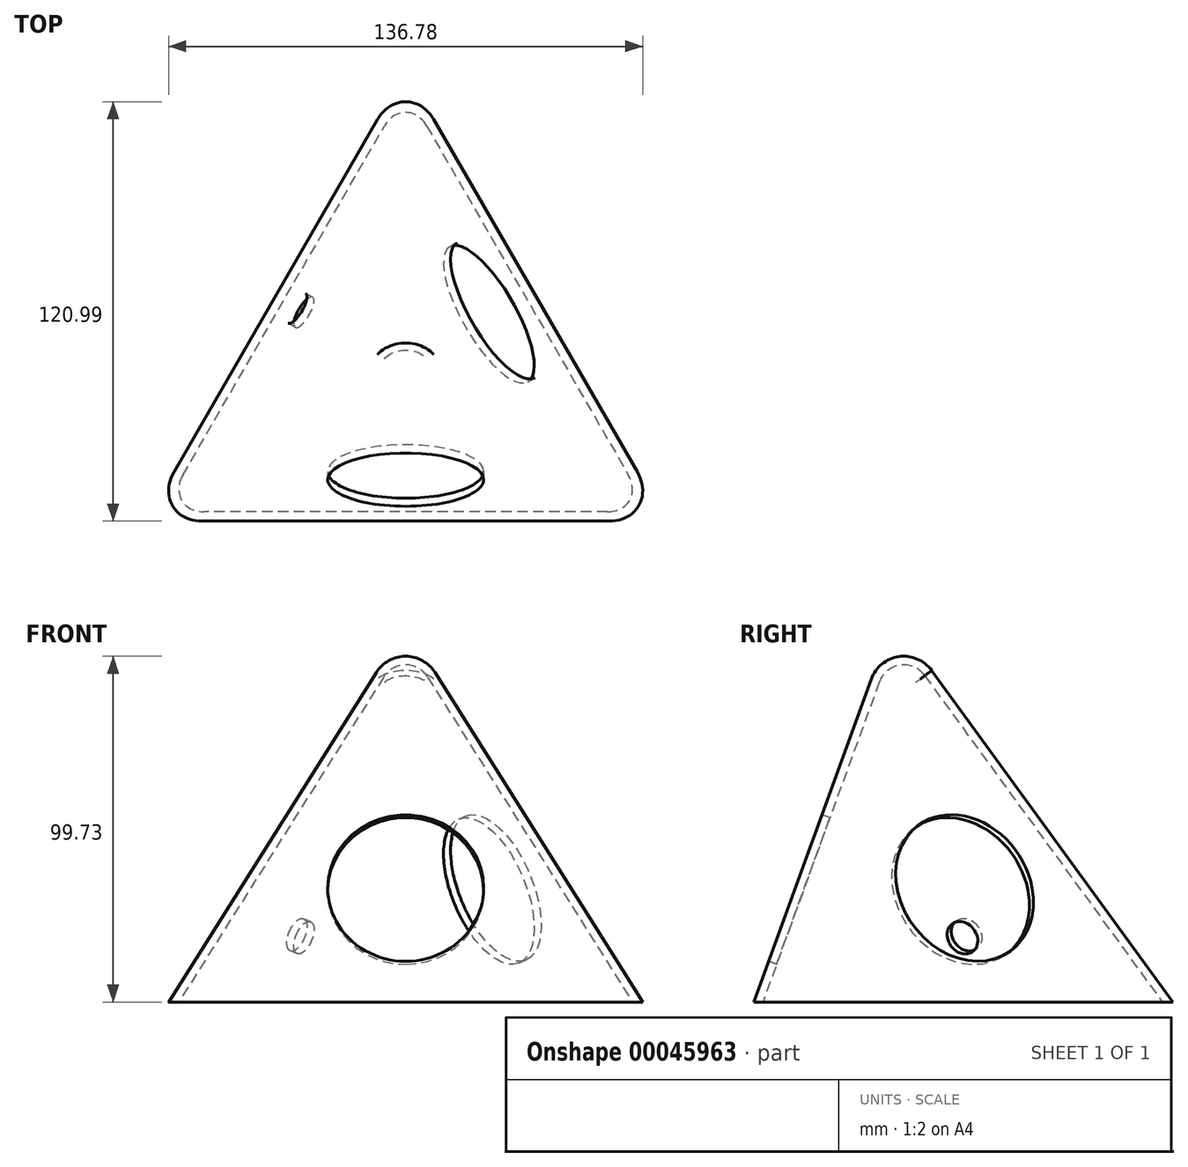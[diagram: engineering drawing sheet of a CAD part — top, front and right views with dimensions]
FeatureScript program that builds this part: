
annotation { "Feature Type Name" : "Feature", "Feature Type Description" : "" }
export const myFeature = defineFeature(function(context is Context, id is Id, definition is map)
    precondition{}
    {
        {
            var Q0;
            Q0=qCreatedBy(makeId("Top.planeOp"),FACE);
            var sketch = newSketch(context, id + "F0", { "sketchPlane" : qUnion([Q0])});
            skCircle(sketch, "E0.cCircle", {"center": v(0, 0) * mm, "radius": 86.6 * mm, "construction": true});
            skLineSegment(sketch, "E0.0", {"start": v(0, 86.6) * mm, "end": v(75, -43.3) * mm});
            skLineSegment(sketch, "E0.1", {"start": v(75, -43.3) * mm, "end": v(-75, -43.3) * mm});
            skLineSegment(sketch, "E0.2", {"start": v(-75, -43.3) * mm, "end": v(0, 86.6) * mm});
            skSolve(sketch);
        }
        {
            var Q0;
            Q0=makeQuery(id+"F0.imprint","IMPRINT",FACE,{"disambiguationData":[TD([[makeQuery(id+"F0.imprint","IMPRINT",EDGE,{"derivedFrom":sQuery(id+"F0.wireOp",EDGE,"E0.0")}),-1.0]])]});
            extrude(context, id + "F1", {"entities" : qUnion([Q0]), "depth" : 200 * mm, "hasDraft" : true, "draftAngle" : 20 * degree, "draftPullDirection" : true});
        }
        {
            var Q0;
            Q0=makeQuery(id+"F1.opExtrude","SWEPT_EDGE",EDGE,{"disambiguationData":[OSD([sQuery(id+"F0.wireOp",EDGE,"E0.0"),sQuery(id+"F0.wireOp",EDGE,"E0.1")])]});
            var Q1;
            Q1=makeQuery(id+"F1.opExtrude","SWEPT_EDGE",EDGE,{"disambiguationData":[OSD([sQuery(id+"F0.wireOp",EDGE,"E0.1"),sQuery(id+"F0.wireOp",EDGE,"E0.2")])]});
            var Q2;
            Q2=makeQuery(id+"F1.opExtrude","SWEPT_EDGE",EDGE,{"disambiguationData":[OSD([sQuery(id+"F0.wireOp",EDGE,"E0.0"),sQuery(id+"F0.wireOp",EDGE,"E0.2")])]});
            fillet(context, id + "F2", {"entities" : qUnion([Q0, Q1, Q2]), "radius" : 10 * mm, "tangentPropagation" : true, "allowEdgeOverflow" : false});
        }
        {
            var Q0;
            Q0=makeQuery(id+"F1.opExtrude","CAP_FACE",FACE,{"disambiguationData":[OSD([sQuery(id+"F0.wireOp",EDGE,"E0.0"),sQuery(id+"F0.wireOp",EDGE,"E0.1"),sQuery(id+"F0.wireOp",EDGE,"E0.2")])],"isStart":true});
            shell(context, id + "F3", {"entities" : qUnion([Q0]), "thickness" : 2.5 * mm});
        }
        {
            var Q0;
            Q0=makeQuery(id+"F1.opExtrude","SWEPT_FACE",FACE,{"disambiguationData":[OSD([sQuery(id+"F0.wireOp",EDGE,"E0.1")])]});
            var sketch = newSketch(context, id + "F4", { "sketchPlane" : qUnion([Q0])});
            skCircle(sketch, "E1", {"center": v(0, 20.2) * mm, "radius": 22.5 * mm});
            skSolve(sketch);
        }
        {
            var Q0;
            Q0=makeQuery(id+"F4.imprint","IMPRINT",FACE,{"disambiguationData":[TD([[makeQuery(id+"F4.imprint","IMPRINT",EDGE,{"derivedFrom":sQuery(id+"F4.wireOp",EDGE,"E1")}),1.0]])]});
            var Q1;
            Q1=makeQuery(id+"F4.imprint","IMPRINT",FACE,{"disambiguationData":[TD([[makeQuery(id+"F4.imprint","IMPRINT",EDGE,{"derivedFrom":sQuery(id+"F4.wireOp",EDGE,"eef62b75-42d1-4a55-b1ed-1820ca84dad8")}),1.0]])]});
            var Q2;
            Q2=makeQuery(id+"F4.imprint","IMPRINT",FACE,{"disambiguationData":[TD([[makeQuery(id+"F4.imprint","IMPRINT",EDGE,{"derivedFrom":sQuery(id+"F4.wireOp",EDGE,"5990fb36-8657-40ea-966b-c35dff720a5a")}),1.0]])]});
            var Q3;
            Q3=makeQuery(id+"F4.imprint","IMPRINT",FACE,{"disambiguationData":[TD([[makeQuery(id+"F4.imprint","IMPRINT",EDGE,{"derivedFrom":sQuery(id+"F4.wireOp",EDGE,"cda414a6-78c4-4a3a-954c-4c09e3075d70")}),1.0]])]});
            extrude(context, id + "F5", {"entities" : qUnion([Q0, Q1, Q2, Q3]), "operationType" : NewBodyOperationType.REMOVE, "endBound" : BoundingType.UP_TO_NEXT, "oppositeDirection" : true, "depth" : 25 * mm});
        }
        {
            var Q0;
            Q0=makeQuery(id+"F1.opExtrude","SWEPT_FACE",FACE,{"disambiguationData":[OSD([sQuery(id+"F0.wireOp",EDGE,"E0.0")])]});
            var sketch = newSketch(context, id + "F6", { "sketchPlane" : qUnion([Q0])});
            skCircle(sketch, "E2", {"center": v(-1.78, 20.23) * mm, "radius": 22.5 * mm});
            skSolve(sketch);
        }
        {
            var Q0;
            Q0=sQuery(id+"F6.wireOp",VERTEX,"E2.center");
            var Q1;
            Q1=makeQuery(id+"F1.opExtrude","SWEPT_BODY",BODY,{"disambiguationData":[OSD([sQuery(id+"F0.wireOp",EDGE,"E0.0"),sQuery(id+"F0.wireOp",EDGE,"E0.1"),sQuery(id+"F0.wireOp",EDGE,"E0.2")])]});
            hole(context, id + "F7", {"style" : HoleStyle.SIMPLE, "holeDiameter" : 45 * mm, "endStyle" : HoleEndStyle.BLIND, "holeDepth" : 20 * mm, "locations" : qUnion([Q0]), "scope" : qUnion([Q1])});
        }
        {
            var Q0;
            Q0=makeQuery(id+"F1.opExtrude","SWEPT_FACE",FACE,{"disambiguationData":[OSD([sQuery(id+"F0.wireOp",EDGE,"E0.2")])]});
            var sketch = newSketch(context, id + "F8", { "sketchPlane" : qUnion([Q0])});
            skPoint(sketch, "E3.centerSnap0", {"position": v(-22.07, 39.78) * mm});
            skCircle(sketch, "E4", {"center": v(1.13, 5.73) * mm, "radius": 5 * mm});
            skSolve(sketch);
        }
        {
            var Q0;
            Q0=sQuery(id+"F8.wireOp",VERTEX,"E4.center");
            var Q1;
            Q1=makeQuery(id+"F1.opExtrude","SWEPT_BODY",BODY,{"disambiguationData":[OSD([sQuery(id+"F0.wireOp",EDGE,"E0.0"),sQuery(id+"F0.wireOp",EDGE,"E0.1"),sQuery(id+"F0.wireOp",EDGE,"E0.2")])]});
            hole(context, id + "F9", {"style" : HoleStyle.SIMPLE, "holeDiameter" : 10 * mm, "endStyle" : HoleEndStyle.BLIND, "holeDepth" : 20 * mm, "locations" : qUnion([Q0]), "scope" : qUnion([Q1])});
        }
    });
